# Revit family: Pultdach_oG_Flachdach
name_source: partatom
category: Windows
units: mm (PartAtom-declared; Revit-internal decimal feet)

## family parameters
Always vertical = No
Cut with Voids When Loaded = Yes
Host = Roof
Room Calculation Point = No
Shared = No

## types (1)
- Pultdach_oG_Flachdach
    - external lenght = -7692 mm  [stored -25.2362 ft]
    - inner length = -7500 mm
    Analytic Construction = <Keine Auswahl>
    Assembly Code = B3020110
    Edition number = 1
    Frame Material = Aluminium (1)
    Glazing Material = Glas
    Height = 754 mm
    Manufacturer = LAMILUX Heinricht Strunz GmbH
    Model = Glasdach PR60
    Product data url = https://www.bimobject.com
    URL = https://www.lamilux.com
    Width = 5000 mm  [stored 16.4042 ft]
    begin wether sheet = -7547 mm
    construction height = 754 mm
    end wether sheet = -7680 mm  [stored -25.1969 ft]
    external width = 5192 mm
    glass roof inclination = 5,00°
    inner length = 7500 mm  [stored 24.6063 ft]
    inner width = 5000 mm  [stored 16.4042 ft]
    length wether sheet = -7682 mm  [stored -25.2034 ft]
    lower frame height = 300 mm
    max. rafter distance = max rafter distance : 1,5 m
    rd = 1570 mm
    rd1 = max rafter distance : 1,0 m
    rd2 = max rafter distance : 1,5 m
    segment distance = 1514 mm
    segment quantity = 5

note: [stored X ft] marks values corroborated as IEEE doubles in the binary element streams (Revit-internal decimal feet)
